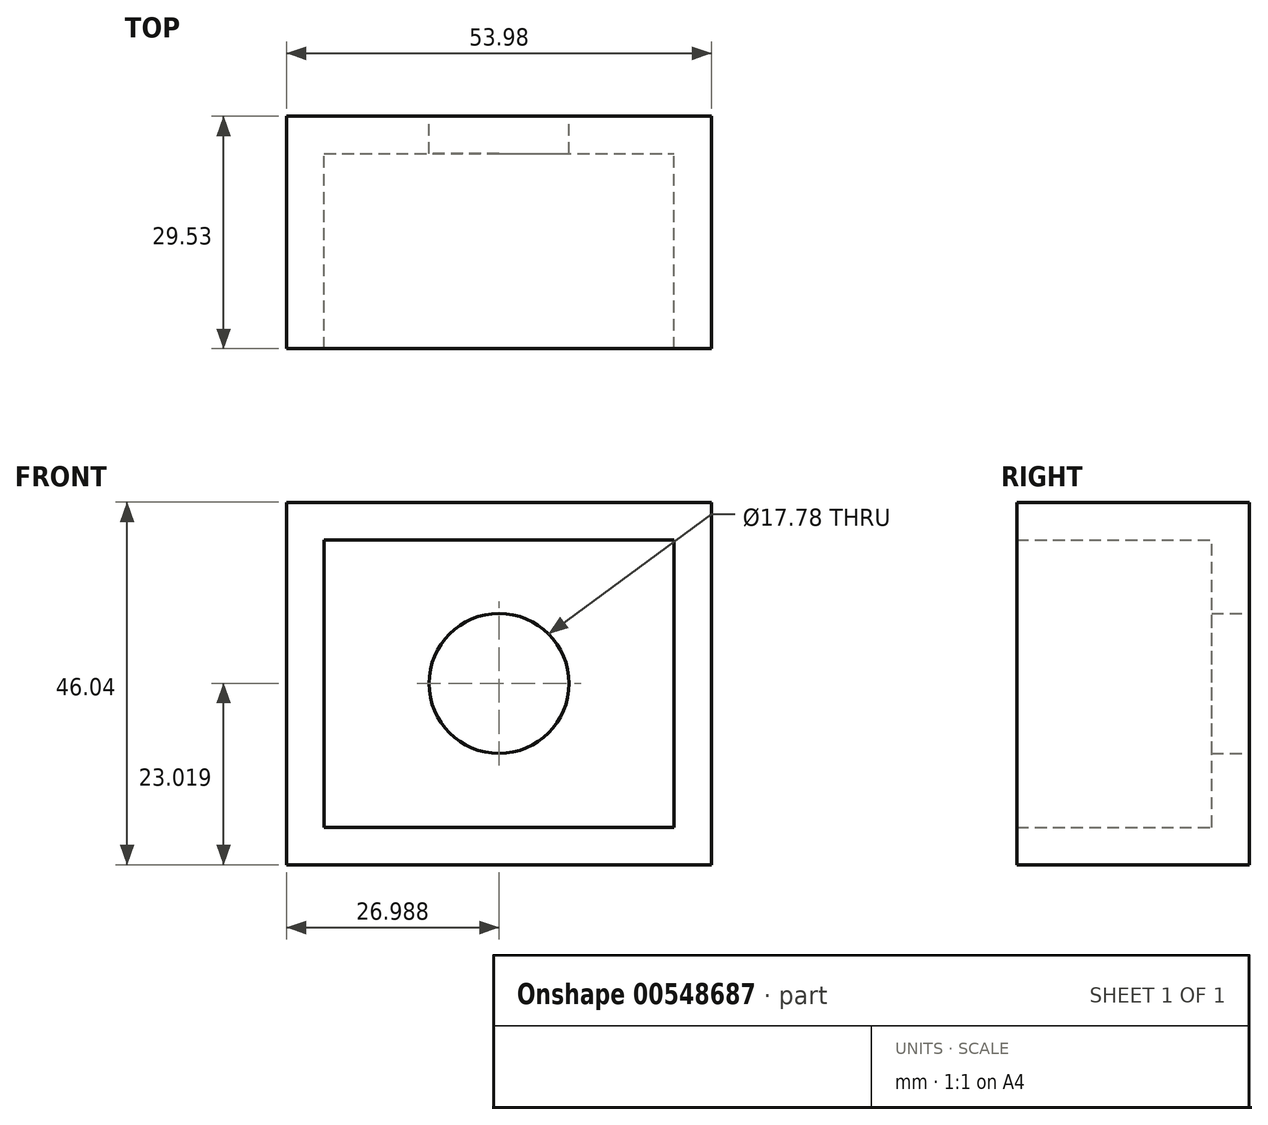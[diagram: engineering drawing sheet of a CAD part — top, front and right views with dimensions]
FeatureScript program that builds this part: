
annotation { "Feature Type Name" : "Feature", "Feature Type Description" : "" }
export const myFeature = defineFeature(function(context is Context, id is Id, definition is map)
    precondition{}
    {
        {
            var Q0;
            Q0=qCreatedBy(makeId("Front.planeOp"),FACE);
            var sketch = newSketch(context, id + "F0", { "sketchPlane" : qUnion([Q0])});
            skLineSegment(sketch, "E0.bottom", {"start": v(0, 0) * mm, "end": v(53.97, 0) * mm});
            skLineSegment(sketch, "E0.top", {"start": v(0, 46.04) * mm, "end": v(53.97, 46.04) * mm});
            skLineSegment(sketch, "E0.left", {"start": v(0, 0) * mm, "end": v(0, 46.04) * mm});
            skLineSegment(sketch, "E0.right", {"start": v(53.97, 0) * mm, "end": v(53.97, 46.04) * mm});
            skSolve(sketch);
        }
        {
            var Q0;
            Q0=makeQuery(id+"F0.imprint","IMPRINT",FACE,{"disambiguationData":[TD([[makeQuery(id+"F0.imprint","IMPRINT",EDGE,{"derivedFrom":sQuery(id+"F0.wireOp",EDGE,"E0.bottom")}),1.0]])]});
            extrude(context, id + "F1", {"entities" : qUnion([Q0]), "depth" : 29.53 * mm, "offsetDistance" : 25.4 * mm});
        }
        {
            var Q0;
            Q0=makeQuery(id+"F1.opExtrude","CAP_FACE",FACE,{"disambiguationData":[OSD([sQuery(id+"F0.wireOp",EDGE,"E0.bottom"),sQuery(id+"F0.wireOp",EDGE,"E0.top"),sQuery(id+"F0.wireOp",EDGE,"E0.left"),sQuery(id+"F0.wireOp",EDGE,"E0.right")])],"isStart":false});
            shell(context, id + "F2", {"entities" : qUnion([Q0]), "thickness" : 4.76 * mm});
        }
        {
            var Q0;
            Q0=makeQuery(id+"F1.opExtrude","CAP_FACE",FACE,{"disambiguationData":[OSD([sQuery(id+"F0.wireOp",EDGE,"E0.bottom"),sQuery(id+"F0.wireOp",EDGE,"E0.top"),sQuery(id+"F0.wireOp",EDGE,"E0.left"),sQuery(id+"F0.wireOp",EDGE,"E0.right")])],"isStart":true});
            var sketch = newSketch(context, id + "F3", { "sketchPlane" : qUnion([Q0])});
            skPoint(sketch, "E1", {"position": v(-26.99, 23.02) * mm});
            skPoint(sketch, "E1.positionSnap0", {"position": v(-53.97, 23.02) * mm});
            skPoint(sketch, "E1.positionSnap1", {"position": v(-26.99, 0) * mm});
            skCircle(sketch, "E2", {"center": v(-26.99, 23.02) * mm, "radius": 7.94 * mm});
            skSolve(sketch);
        }
        {
            var Q0;
            Q0=sQuery(id+"F3.wireOp",VERTEX,"E1");
            var Q1;
            Q1=makeQuery(id+"F1.opExtrude","SWEPT_BODY",BODY,{"disambiguationData":[OSD([sQuery(id+"F0.wireOp",EDGE,"E0.bottom"),sQuery(id+"F0.wireOp",EDGE,"E0.top"),sQuery(id+"F0.wireOp",EDGE,"E0.left"),sQuery(id+"F0.wireOp",EDGE,"E0.right")])]});
            hole(context, id + "F4", {"style" : HoleStyle.SIMPLE, "endStyle" : HoleEndStyle.BLIND, "holeDiameter" : 17.78 * mm, "holeDepth" : 25.4 * mm, "isTappedThrough" : true, "tappedDepth" : 12.7 * mm, "tapClearance" : 3, "locations" : qUnion([Q0]), "scope" : qUnion([Q1])});
        }
    });
